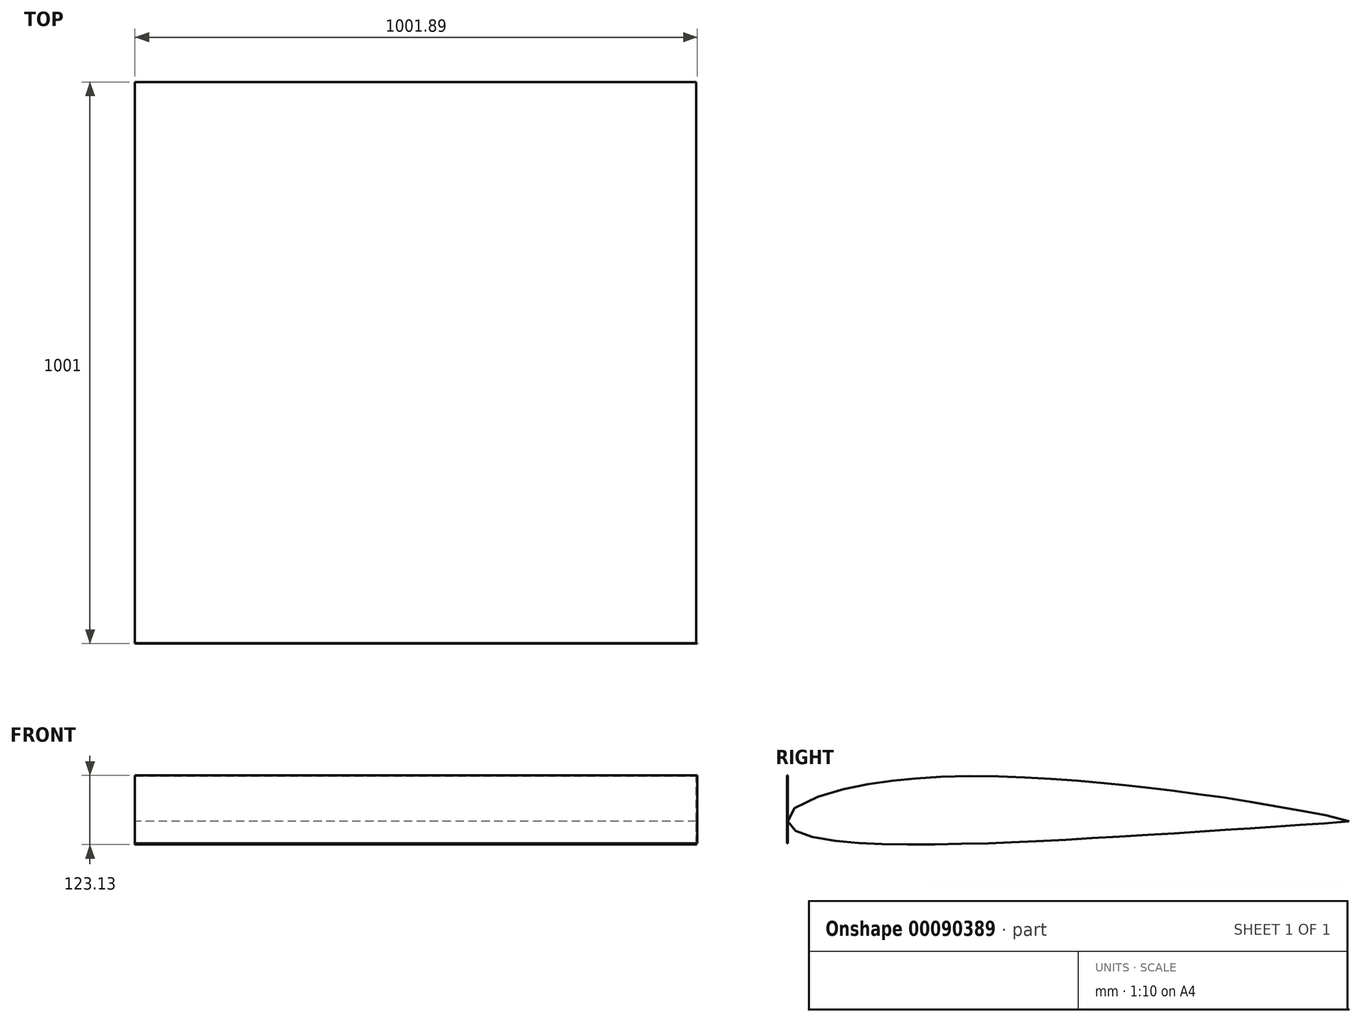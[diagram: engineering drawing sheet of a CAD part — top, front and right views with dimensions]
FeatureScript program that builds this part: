
annotation { "Feature Type Name" : "Feature", "Feature Type Description" : "" }
export const myFeature = defineFeature(function(context is Context, id is Id, definition is map)
    precondition{}
    {
        {
            var Q0;
            Q0=qCreatedBy(makeId("Right.planeOp"),FACE);
            var sketch = newSketch(context, id + "F0", { "sketchPlane" : qUnion([Q0])});
            skLineSegment(sketch, "E0", {"start": v(0, 0) * mm, "end": v(1000, 0) * mm, "construction": true});
            skFitSpline(sketch, "E1", {"points": [v(0, 0) * mm, v(3.2, 13.06) * mm, v(15.34, 25.24) * mm, v(58.15, 45.18) * mm, v(99.86, 57.07) * mm, v(138.64, 65.12) * mm, v(181.08, 71.52) * mm, v(211.27, 74.81) * mm, v(252.43, 77.74) * mm, v(295.23, 79.75) * mm, v(352.3, 80.12) * mm, v(399.5, 79.02) * mm, v(443.6, 76.64) * mm, v(488.05, 74.26) * mm, v(532.68, 70.79) * mm, v(577.14, 66.76) * mm, v(604.4, 64.02) * mm, v(636.6, 60.18) * mm, v(672.63, 55.79) * mm, v(713.6, 50.67) * mm, v(755.68, 45) * mm, v(799.22, 38.6) * mm, v(852.64, 29.81) * mm, v(889.77, 23.04) * mm, v(931.48, 15.73) * mm, v(966.42, 8.96) * mm, v(1000, 0) * mm], "startDerivative": vector(0, 733.33) * mm, "endDerivative": vector(433.82, -233.49) * mm});
            skFitSpline(sketch, "E2", {"points": [v(0, 0) * mm, v(1.08, -5.36) * mm, v(9.81, -14.55) * mm, v(29.01, -23.88) * mm, v(47.62, -29.2) * mm, v(83.57, -35.12) * mm, v(117.4, -38.32) * mm, v(152.86, -40.45) * mm, v(190.56, -41.42) * mm, v(234.46, -41.7) * mm, v(281.94, -41.03) * mm, v(325.06, -40.06) * mm, v(370.83, -38.83) * mm, v(400.37, -37.46) * mm, v(440.34, -35.82) * mm, v(497.51, -33.07) * mm, v(540.41, -30.51) * mm, v(586.88, -27.77) * mm, v(638.83, -24.75) * mm, v(683.65, -22) * mm, v(725, -19.44) * mm, v(765.51, -16.6) * mm, v(804.66, -13.86) * mm, v(846.28, -11.3) * mm, v(886.61, -8.56) * mm, v(924.04, -5.83) * mm, v(961.6, -3.59) * mm, v(1000, 0) * mm], "startDerivative": vector(0, -299.02) * mm, "endDerivative": vector(970.9, 129.72) * mm});
            skSolve(sketch);
        }
        {
            var Q0;
            Q0 = qSketchRegion(id + "F0", true);
            extrude(context, id + "F1", {"entities" : qUnion([Q0]), "depth" : 1000 * mm});
        }
        {
            var Q0;
            Q0=qCreatedBy(makeId("Front.planeOp"),FACE);
            var sketch = newSketch(context, id + "F2", { "sketchPlane" : qUnion([Q0])});
            skLineSegment(sketch, "E3.bottom", {"start": v(0, 81.4) * mm, "end": v(1001.9, 81.4) * mm});
            skLineSegment(sketch, "E3.top", {"start": v(0, -39.33) * mm, "end": v(1001.9, -39.33) * mm});
            skLineSegment(sketch, "E3.left", {"start": v(0, 81.4) * mm, "end": v(0, -39.33) * mm});
            skLineSegment(sketch, "E3.right", {"start": v(1001.9, 81.4) * mm, "end": v(1001.9, -39.33) * mm});
            skSolve(sketch);
        }
        {
            var Q0;
            Q0 = qSketchRegion(id + "F2", true);
            extrude(context, id + "F3", {"entities" : qUnion([Q0]), "depth" : 1 * mm});
        }
    });
